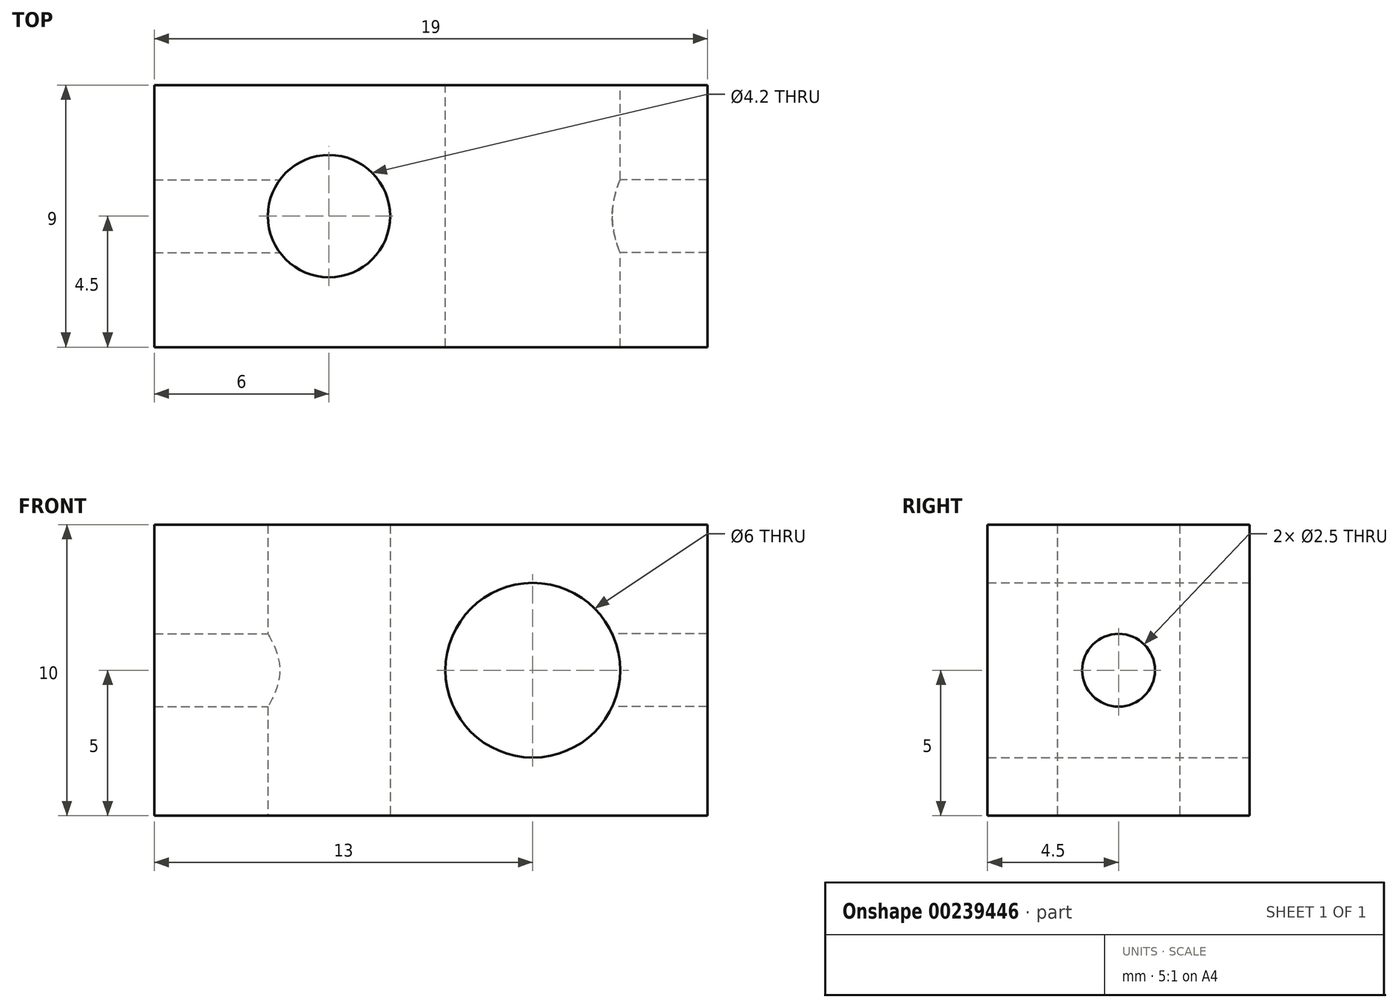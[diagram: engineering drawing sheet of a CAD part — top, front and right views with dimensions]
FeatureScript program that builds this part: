
annotation { "Feature Type Name" : "Feature", "Feature Type Description" : "" }
export const myFeature = defineFeature(function(context is Context, id is Id, definition is map)
    precondition{}
    {
        {
            var Q0;
            Q0=qCreatedBy(makeId("Top.planeOp"),FACE);
            var sketch = newSketch(context, id + "F0", { "sketchPlane" : qUnion([Q0])});
            skLineSegment(sketch, "E0.bottom", {"start": v(9.5, 4.5) * mm, "end": v(-9.5, 4.5) * mm});
            skLineSegment(sketch, "E0.top", {"start": v(9.5, -4.5) * mm, "end": v(-9.5, -4.5) * mm});
            skLineSegment(sketch, "E0.left", {"start": v(9.5, 4.5) * mm, "end": v(9.5, -4.5) * mm});
            skLineSegment(sketch, "E0.right", {"start": v(-9.5, 4.5) * mm, "end": v(-9.5, -4.5) * mm});
            skPoint(sketch, "E0.middle", {"position": v(0, 0) * mm});
            skSolve(sketch);
        }
        {
            var Q0;
            Q0 = qSketchRegion(id + "F0", true);
            extrude(context, id + "F1", {"entities" : qUnion([Q0]), "depth" : 10 * mm, "symmetric" : true});
        }
        {
            var Q0;
            Q0=makeQuery(id+"F1.opExtrude","CAP_FACE",FACE,{"disambiguationData":[OSD([sQuery(id+"F0.wireOp",EDGE,"E0.bottom"),sQuery(id+"F0.wireOp",EDGE,"E0.top"),sQuery(id+"F0.wireOp",EDGE,"E0.left"),sQuery(id+"F0.wireOp",EDGE,"E0.right")])],"isStart":false});
            var sketch = newSketch(context, id + "F2", { "sketchPlane" : qUnion([Q0])});
            skPoint(sketch, "E1", {"position": v(-3.5, 0) * mm});
            skSolve(sketch);
        }
        {
            var Q0;
            Q0=sQuery(id+"F2.wireOp",VERTEX,"E1");
            var Q1;
            Q1=makeQuery(id+"F1.opExtrude","SWEPT_BODY",BODY,{"disambiguationData":[OSD([sQuery(id+"F0.wireOp",EDGE,"E0.bottom"),sQuery(id+"F0.wireOp",EDGE,"E0.top"),sQuery(id+"F0.wireOp",EDGE,"E0.left"),sQuery(id+"F0.wireOp",EDGE,"E0.right")])]});
            hole(context, id + "F3", {"style" : HoleStyle.SIMPLE, "endStyle" : HoleEndStyle.THROUGH, "standardTappedOrClearance" : lookupTablePath({ "standard" : "ISO", "engagement" : "75%", "pitch" : "0.8 mm", "size" : "M5", "type" : "Tapped" }), "standardBlindInLast" : lookupTablePath({ "standard" : "ISO", "engagement" : "75%", "pitch" : "0.8 mm", "size" : "M5", "type" : "Tapped" }), "holeDiameter" : 4.2 * mm, "locations" : qUnion([Q0]), "scope" : qUnion([Q1]), "isTappedThrough" : true, "majorDiameter" : 5 * mm, "showTappedDepth" : true, "startStyle" : HoleStartStyle.PART});
        }
        {
            var Q0;
            Q0=makeQuery(id+"F1.opExtrude","SWEPT_FACE",FACE,{"disambiguationData":[OSD([sQuery(id+"F0.wireOp",EDGE,"E0.top")])]});
            var sketch = newSketch(context, id + "F4", { "sketchPlane" : qUnion([Q0])});
            skPoint(sketch, "E2", {"position": v(3.5, 0) * mm});
            skSolve(sketch);
        }
        {
            var Q0;
            Q0=sQuery(id+"F4.wireOp",VERTEX,"E2");
            var Q1;
            Q1=makeQuery(id+"F1.opExtrude","SWEPT_BODY",BODY,{"disambiguationData":[OSD([sQuery(id+"F0.wireOp",EDGE,"E0.bottom"),sQuery(id+"F0.wireOp",EDGE,"E0.top"),sQuery(id+"F0.wireOp",EDGE,"E0.left"),sQuery(id+"F0.wireOp",EDGE,"E0.right")])]});
            hole(context, id + "F5", {"style" : HoleStyle.SIMPLE, "endStyle" : HoleEndStyle.THROUGH, "standardTappedOrClearance" : lookupTablePath({ "standard" : "ISO", "size" : "6", "type" : "Drilled" }), "standardBlindInLast" : lookupTablePath({ "standard" : "ISO", "size" : "6", "type" : "Drilled" }), "holeDiameter" : 6 * mm, "locations" : qUnion([Q0]), "scope" : qUnion([Q1]), "isTappedThrough" : true, "startStyle" : HoleStartStyle.PART});
        }
        {
            var Q0;
            Q0=makeQuery(id+"F1.opExtrude","SWEPT_FACE",FACE,{"disambiguationData":[OSD([sQuery(id+"F0.wireOp",EDGE,"E0.left")])]});
            var sketch = newSketch(context, id + "F6", { "sketchPlane" : qUnion([Q0])});
            skPoint(sketch, "E3", {"position": v(0, 0) * mm});
            skSolve(sketch);
        }
        {
            var Q0;
            Q0=sQuery(id+"F6.wireOp",VERTEX,"E3");
            var Q1;
            Q1=makeQuery(id+"F1.opExtrude","SWEPT_BODY",BODY,{"disambiguationData":[OSD([sQuery(id+"F0.wireOp",EDGE,"E0.bottom"),sQuery(id+"F0.wireOp",EDGE,"E0.top"),sQuery(id+"F0.wireOp",EDGE,"E0.left"),sQuery(id+"F0.wireOp",EDGE,"E0.right")])]});
            hole(context, id + "F7", {"style" : HoleStyle.SIMPLE, "endStyle" : HoleEndStyle.BLIND, "standardTappedOrClearance" : lookupTablePath({ "standard" : "ISO", "engagement" : "75%", "pitch" : "0.5 mm", "size" : "M3", "type" : "Tapped" }), "standardBlindInLast" : lookupTablePath({ "standard" : "ISO", "engagement" : "75%", "pitch" : "0.5 mm", "size" : "M3", "type" : "Tapped" }), "holeDiameter" : 2.5 * mm, "holeDepth" : 5 * mm, "locations" : qUnion([Q0]), "scope" : qUnion([Q1]), "majorDiameter" : 3 * mm, "startStyle" : HoleStartStyle.PART});
        }
        {
            var Q0;
            Q0=makeQuery(id+"F1.opExtrude","SWEPT_FACE",FACE,{"disambiguationData":[OSD([sQuery(id+"F0.wireOp",EDGE,"E0.right")])]});
            var sketch = newSketch(context, id + "F8", { "sketchPlane" : qUnion([Q0])});
            skPoint(sketch, "E4", {"position": v(0, 0) * mm});
            skSolve(sketch);
        }
        {
            var Q0;
            Q0=sQuery(id+"F8.wireOp",VERTEX,"E4");
            var Q1;
            Q1=makeQuery(id+"F1.opExtrude","SWEPT_BODY",BODY,{"disambiguationData":[OSD([sQuery(id+"F0.wireOp",EDGE,"E0.bottom"),sQuery(id+"F0.wireOp",EDGE,"E0.top"),sQuery(id+"F0.wireOp",EDGE,"E0.left"),sQuery(id+"F0.wireOp",EDGE,"E0.right")])]});
            hole(context, id + "F9", {"style" : HoleStyle.SIMPLE, "endStyle" : HoleEndStyle.BLIND, "standardTappedOrClearance" : lookupTablePath({ "standard" : "ISO", "engagement" : "75%", "pitch" : "0.5 mm", "size" : "M3", "type" : "Tapped" }), "standardBlindInLast" : lookupTablePath({ "standard" : "ISO", "engagement" : "75%", "pitch" : "0.5 mm", "size" : "M3", "type" : "Tapped" }), "holeDiameter" : 2.5 * mm, "holeDepth" : 6 * mm, "locations" : qUnion([Q0]), "scope" : qUnion([Q1]), "majorDiameter" : 3 * mm, "startStyle" : HoleStartStyle.PART});
        }
    });
